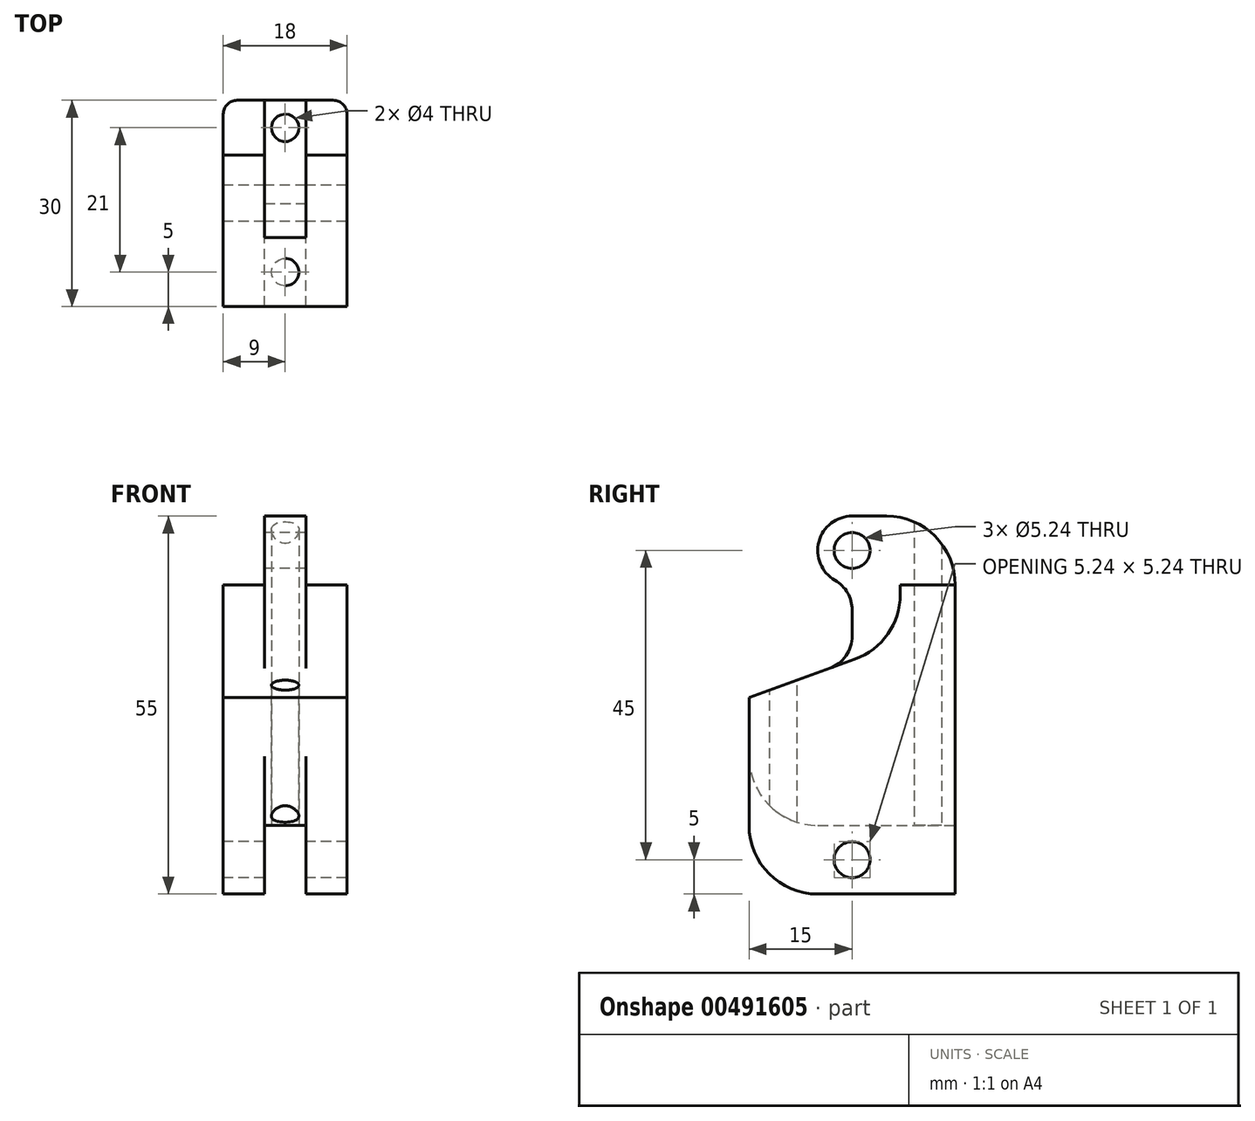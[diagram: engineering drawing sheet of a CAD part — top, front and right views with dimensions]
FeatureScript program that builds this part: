
annotation { "Feature Type Name" : "Feature", "Feature Type Description" : "" }
export const myFeature = defineFeature(function(context is Context, id is Id, definition is map)
    precondition{}
    {
        {
            var Q0;
            Q0=qCreatedBy(makeId("Front.planeOp"),FACE);
            var sketch = newSketch(context, id + "F0", { "sketchPlane" : qUnion([Q0])});
            skLineSegment(sketch, "E0.bottom", {"start": v(9, 17.5) * mm, "end": v(3, 17.5) * mm});
            skLineSegment(sketch, "E0.top", {"start": v(3, -17.5) * mm, "end": v(-3, -17.5) * mm});
            skLineSegment(sketch, "E0.left", {"start": v(9, 17.5) * mm, "end": v(9, -17.5) * mm});
            skLineSegment(sketch, "E0.right", {"start": v(-9, 17.5) * mm, "end": v(-9, -17.5) * mm});
            skPoint(sketch, "E0.middle", {"position": v(0, 0) * mm});
            skLineSegment(sketch, "E1.bottom", {"start": v(3, 27.5) * mm, "end": v(-3, 27.5) * mm});
            skLineSegment(sketch, "E1.left", {"start": v(3, 27.5) * mm, "end": v(3, 17.5) * mm});
            skLineSegment(sketch, "E1.right", {"start": v(-3, 27.5) * mm, "end": v(-3, 17.5) * mm});
            skPoint(sketch, "E1.middle", {"position": v(0, 17.5) * mm});
            skLineSegment(sketch, "E2.top", {"start": v(-9, -27.5) * mm, "end": v(-3, -27.5) * mm});
            skLineSegment(sketch, "E2.right", {"start": v(-3, -17.5) * mm, "end": v(-3, -27.5) * mm});
            skLineSegment(sketch, "E3.MirrorCS", {"start": v(3, -17.5) * mm, "end": v(3, -27.5) * mm});
            skLineSegment(sketch, "E4.MirrorCS", {"start": v(9, -27.5) * mm, "end": v(3, -27.5) * mm});
            skLineSegment(sketch, "E5.MirrorCS", {"start": v(9, -17.5) * mm, "end": v(9, -27.5) * mm});
            skLineSegment(sketch, "E6.trimOffspring", {"start": v(-3, 17.5) * mm, "end": v(-9, 17.5) * mm});
            skLineSegment(sketch, "E7", {"start": v(-9, -17.5) * mm, "end": v(-9, -27.5) * mm});
            skSolve(sketch);
        }
        {
            var Q0;
            Q0=makeQuery(id+"F0.imprint","IMPRINT",FACE,{"disambiguationData":[TD([[makeQuery(id+"F0.imprint","IMPRINT",EDGE,{"derivedFrom":sQuery(id+"F0.wireOp",EDGE,"E0.bottom")}),1.0]])]});
            extrude(context, id + "F1", {"entities" : qUnion([Q0]), "depth" : 30 * mm, "symmetric" : true});
        }
        {
            var Q0;
            Q0=makeQuery(id+"F1.opExtrude","SWEPT_FACE",FACE,{"disambiguationData":[OSD([sQuery(id+"F0.wireOp",EDGE,"E1.right")])]});
            var sketch = newSketch(context, id + "F2", { "sketchPlane" : qUnion([Q0])});
            skLineSegment(sketch, "E8", {"start": v(0, 17.5) * mm, "end": v(0, 27.5) * mm});
            skCircle(sketch, "E9", {"center": v(0, 22.5) * mm, "radius": 2.62 * mm});
            skSolve(sketch);
        }
        {
            var Q0;
            Q0 = qSketchRegion(id + "F2", true);
            extrude(context, id + "F3", {"entities" : qUnion([Q0]), "operationType" : NewBodyOperationType.REMOVE, "oppositeDirection" : true, "depth" : 6 * mm});
        }
        {
            var Q0;
            Q0=makeQuery(id+"F1.opExtrude","SWEPT_FACE",FACE,{"disambiguationData":[OSD([sQuery(id+"F0.wireOp",EDGE,"E0.right"),sQuery(id+"F0.wireOp",EDGE,"E7")])]});
            var sketch = newSketch(context, id + "F4", { "sketchPlane" : qUnion([Q0])});
            skPoint(sketch, "E10.endSnap0", {"position": v(0, -27.5) * mm});
            skCircle(sketch, "E11", {"center": v(0, -22.5) * mm, "radius": 2.62 * mm});
            skLineSegment(sketch, "E12", {"start": v(0, -27.5) * mm, "end": v(0, -22.5) * mm});
            skSolve(sketch);
        }
        {
            var Q0;
            Q0 = qSketchRegion(id + "F4", true);
            extrude(context, id + "F5", {"entities" : qUnion([Q0]), "operationType" : NewBodyOperationType.REMOVE, "oppositeDirection" : true, "depth" : 18 * mm});
        }
        {
            var Q0;
            Q0=makeQuery(id+"F1.opExtrude","CAP_EDGE",EDGE,{"disambiguationData":[OSD([sQuery(id+"F0.wireOp",EDGE,"E1.bottom")])],"isStart":true});
            var Q1;
            Q1=makeQuery(id+"F1.opExtrude","CAP_EDGE",EDGE,{"disambiguationData":[OSD([sQuery(id+"F0.wireOp",EDGE,"E1.bottom")])],"isStart":false});
            var Q2;
            Q2=makeQuery(id+"F1.opExtrude","CAP_EDGE",EDGE,{"disambiguationData":[OSD([sQuery(id+"F0.wireOp",EDGE,"E4.MirrorCS")])],"isStart":false});
            var Q3;
            Q3=makeQuery(id+"F1.opExtrude","CAP_EDGE",EDGE,{"disambiguationData":[OSD([sQuery(id+"F0.wireOp",EDGE,"E2.top")])],"isStart":false});
            fillet(context, id + "F6", {"entities" : qUnion([Q0, Q1, Q2, Q3]), "radius" : 10 * mm, "tangentPropagation" : true, "allowEdgeOverflow" : false});
        }
        {
            var Q0;
            Q0=makeQuery(id+"F1.opExtrude","SWEPT_FACE",FACE,{"disambiguationData":[OSD([sQuery(id+"F0.wireOp",EDGE,"E0.left"),sQuery(id+"F0.wireOp",EDGE,"E5.MirrorCS")])]});
            var sketch = newSketch(context, id + "F7", { "sketchPlane" : qUnion([Q0])});
            skPoint(sketch, "E13.endSnap0", {"position": v(0, 17.5) * mm});
            skLineSegment(sketch, "E14", {"start": v(-15, 17.5) * mm, "end": v(-15, 1.08) * mm});
            skLineSegment(sketch, "E15", {"start": v(-15, 17.5) * mm, "end": v(7, 17.5) * mm});
            skLineSegment(sketch, "E16", {"start": v(-15, 1.08) * mm, "end": v(15, 1.08) * mm});
            skLineSegment(sketch, "E17", {"start": v(-15, 1.08) * mm, "end": v(0.42, 6.7) * mm});
            skLineSegment(sketch, "E18", {"start": v(7, 17.5) * mm, "end": v(7, 16.09) * mm});
            skPoint(sketch, "E19.visualSharp", {"position": v(7, 9.09) * mm});
            skArc(sketch, "E19.filletArc", {"start": v(0.42, 6.7) * mm, "mid": v(5.2, 10.35) * mm, "end": v(7, 16.09) * mm});
            skSolve(sketch);
        }
        {
            var Q0;
            Q0=makeQuery(id+"F1.opExtrude","SWEPT_FACE",FACE,{"disambiguationData":[OSD([sQuery(id+"F0.wireOp",EDGE,"E0.right"),sQuery(id+"F0.wireOp",EDGE,"E7")])]});
            var sketch = newSketch(context, id + "F8", { "sketchPlane" : qUnion([Q0])});
            skLineSegment(sketch, "E20", {"start": v(-0.42, 6.7) * mm, "end": v(15, 1.08) * mm});
            skLineSegment(sketch, "E21", {"start": v(15, 1.08) * mm, "end": v(15, 17.5) * mm});
            skLineSegment(sketch, "E22", {"start": v(15, 1.08) * mm, "end": v(-15, 1.08) * mm});
            skLineSegment(sketch, "E23", {"start": v(15, 17.5) * mm, "end": v(-7, 17.5) * mm});
            skLineSegment(sketch, "E24", {"start": v(-7, 17.5) * mm, "end": v(-7, 16.09) * mm});
            skPoint(sketch, "E25.visualSharp", {"position": v(-7, 9.09) * mm});
            skArc(sketch, "E25.filletArc", {"start": v(-7, 16.09) * mm, "mid": v(-5.2, 10.35) * mm, "end": v(-0.42, 6.7) * mm});
            skSolve(sketch);
        }
        {
            var Q0;
            Q0=makeQuery(id+"F8.imprint","IMPRINT",FACE,{"disambiguationData":[TD([[makeQuery(id+"F8.imprint","IMPRINT",EDGE,{"derivedFrom":sQuery(id+"F8.wireOp",EDGE,"E20")}),1.0]])]});
            extrude(context, id + "F9", {"entities" : qUnion([Q0]), "operationType" : NewBodyOperationType.REMOVE, "oppositeDirection" : true, "depth" : 6 * mm});
        }
        {
            var Q0;
            Q0=makeQuery(id+"F7.imprint","IMPRINT",FACE,{"disambiguationData":[TD([[makeQuery(id+"F7.imprint","IMPRINT",EDGE,{"derivedFrom":sQuery(id+"F7.wireOp",EDGE,"E14")}),1.0]])]});
            extrude(context, id + "F10", {"entities" : qUnion([Q0]), "operationType" : NewBodyOperationType.REMOVE, "oppositeDirection" : true, "depth" : 6 * mm});
        }
        {
            var Q0;
            Q0=makeQuery(id+"F1.opExtrude","CAP_EDGE",EDGE,{"disambiguationData":[OSD([sQuery(id+"F0.wireOp",EDGE,"E0.left"),sQuery(id+"F0.wireOp",EDGE,"E5.MirrorCS")])],"isStart":true});
            var Q1;
            Q1=makeQuery(id+"F1.opExtrude","CAP_EDGE",EDGE,{"disambiguationData":[OSD([sQuery(id+"F0.wireOp",EDGE,"E0.right"),sQuery(id+"F0.wireOp",EDGE,"E7")])],"isStart":true});
            fillet(context, id + "F11", {"entities" : qUnion([Q0, Q1]), "radius" : 2 * mm, "tangentPropagation" : true, "allowEdgeOverflow" : false});
        }
        {
            var Q0;
            Q0=makeQuery(id+"F9.boolean.opBoolean","MERGE",FACE,{"derivedFrom":[makeQuery(id+"F1.opExtrude","SWEPT_FACE",FACE,{"disambiguationData":[OSD([sQuery(id+"F0.wireOp",EDGE,"E1.right")])]}),makeQuery(id+"F9.opExtrude","CAP_FACE",FACE,{"disambiguationData":[OSD([sQuery(id+"F8.wireOp",EDGE,"E20"),sQuery(id+"F8.wireOp",EDGE,"E21"),sQuery(id+"F8.wireOp",EDGE,"E23"),sQuery(id+"F8.wireOp",EDGE,"E24"),sQuery(id+"F8.wireOp",EDGE,"E25.filletArc")])],"isStart":false})]});
            var sketch = newSketch(context, id + "F12", { "sketchPlane" : qUnion([Q0])});
            skLineSegment(sketch, "E26", {"start": v(0, 27.5) * mm, "end": v(0, 25.12) * mm});
            skCircle(sketch, "E27", {"center": v(0, 22.5) * mm, "radius": 5 * mm});
            skLineSegment(sketch, "E28", {"start": v(0, 22.5) * mm, "end": v(5, 22.5) * mm});
            skLineSegment(sketch, "E29", {"start": v(5, 22.5) * mm, "end": v(5, 4.72) * mm});
            skSolve(sketch);
        }
        {
            var Q0;
            {var subQ1=sQuery(id+"F12.wireOp",EDGE,"E29");Q0=makeQuery(id+"F12.imprint","IMPRINT",FACE,{"disambiguationData":[TD([[makeQuery(id+"F12.imprint","IMPRINT",EDGE,{"derivedFrom":subQ1}),1.0]])]});}
            extrude(context, id + "F13", {"entities" : qUnion([Q0]), "operationType" : NewBodyOperationType.REMOVE, "oppositeDirection" : true, "depth" : 6 * mm});
        }
        {
            var Q0;
            Q0=makeQuery(id+"F1.opExtrude","SWEPT_FACE",FACE,{"disambiguationData":[OSD([sQuery(id+"F0.wireOp",EDGE,"E0.top")])]});
            var sketch = newSketch(context, id + "F14", { "sketchPlane" : qUnion([Q0])});
            skSolve(sketch);
        }
        {
            var Q0;
            Q0=makeQuery(id+"F1.opExtrude","CAP_EDGE",EDGE,{"disambiguationData":[OSD([sQuery(id+"F0.wireOp",EDGE,"E0.top")])],"isStart":false});
            fillet(context, id + "F15", {"entities" : qUnion([Q0]), "radius" : 10 * mm, "tangentPropagation" : true, "allowEdgeOverflow" : false});
        }
        {
            var Q0;
            {var subQ0=sQuery(id+"F8.wireOp",EDGE,"E20");Q0=makeQuery(id+"F13.boolean.opBoolean","MERGE",FACE,{"derivedFrom":[makeQuery(id+"F9.boolean.opBoolean","COPY",FACE,{"derivedFrom":makeQuery(id+"F9.opExtrude","SWEPT_FACE",FACE,{"disambiguationData":[OSD([subQ0])]})}),makeQuery(id+"F10.boolean.opBoolean","COPY",FACE,{"derivedFrom":makeQuery(id+"F10.opExtrude","SWEPT_FACE",FACE,{"disambiguationData":[OSD([sQuery(id+"F7.wireOp",EDGE,"E17")])]})}),makeQuery(id+"F13.opExtrude","SWEPT_FACE",FACE,{"disambiguationData":[OSD([subQ0])]})]});}
            var sketch = newSketch(context, id + "F16", { "sketchPlane" : qUnion([Q0])});
            skLineSegment(sketch, "E30", {"start": v(0, -3.08) * mm, "end": v(0, -13.73) * mm});
            skSolve(sketch);
        }
        {
            var Q0;
            Q0=makeQuery(id+"F13.boolean.opBoolean","COPY",EDGE,{"derivedFrom":makeQuery(id+"F13.opExtrude","SWEPT_EDGE",EDGE,{"disambiguationData":[OSD([sQuery(id+"F12.wireOp",EDGE,"E27"),sQuery(id+"F12.wireOp",EDGE,"E28"),sQuery(id+"F12.wireOp",EDGE,"E29")])]})});
            cPlane(context, id + "F17", {"entities" : qUnion([Q0]), "cplaneType" : CPlaneType.LINE_ANGLE, "offset" : 25 * mm, "angle" : 90 * degree, "width" : 150 * mm, "height" : 150 * mm});
        }
        {
            var Q0;
            Q0=qCreatedBy(id+"F17.planeOp",FACE);
            var sketch = newSketch(context, id + "F18", { "sketchPlane" : qUnion([Q0])});
            skLineSegment(sketch, "E31", {"start": v(0, -5) * mm, "end": v(0, -15) * mm});
            skCircle(sketch, "E32", {"center": v(0, -10) * mm, "radius": 2 * mm});
            skSolve(sketch);
        }
        {
            var Q0;
            Q0 = qSketchRegion(id + "F18", true);
            extrude(context, id + "F19", {"entities" : qUnion([Q0]), "operationType" : NewBodyOperationType.REMOVE, "endBound" : BoundingType.THROUGH_ALL, "oppositeDirection" : true, "depth" : 40 * mm});
        }
        {
            var Q0;
            {var subQ0=sQuery(id+"F0.wireOp",EDGE,"E0.top");Q0=makeQuery(id+"F14.imprint","IMPRINT",FACE,{"disambiguationData":[TD([[makeQuery(id+"F14.imprint","IMPRINT",EDGE,{"derivedFrom":makeQuery(id+"F1.opExtrude","CAP_EDGE",EDGE,{"disambiguationData":[OSD([subQ0])],"isStart":true})}),-1.0]])]});}
            var sketch = newSketch(context, id + "F20", { "sketchPlane" : qUnion([Q0])});
            skLineSegment(sketch, "E33", {"start": v(0, -15) * mm, "end": v(0, -11) * mm});
            skCircle(sketch, "E34", {"center": v(0, -11) * mm, "radius": 2 * mm});
            skLineSegment(sketch, "E35", {"start": v(0, -11) * mm, "end": v(0, -7.51) * mm});
            skSolve(sketch);
        }
        {
            var Q0;
            {var subQ0=sQuery(id+"F20.wireOp",EDGE,"E35");var subQ1=sQuery(id+"F20.wireOp",EDGE,"E33");var subQ2=makeQuery(id+"F20.imprint","INTERSECT",VERTEX,{"derivedFrom":[subQ1,subQ0]});Q0=makeQuery(id+"F20.imprint","IMPRINT",FACE,{"disambiguationData":[TD([[makeQuery(id+"F20.imprint","IMPRINT",EDGE,{"disambiguationData":[TD([[subQ2,1.0]])],"derivedFrom":subQ1}),1.0]])]});}
            var Q1;
            {var subQ0=sQuery(id+"F20.wireOp",EDGE,"E35");var subQ1=sQuery(id+"F20.wireOp",EDGE,"E33");var subQ2=makeQuery(id+"F20.imprint","INTERSECT",VERTEX,{"derivedFrom":[subQ1,subQ0]});Q1=makeQuery(id+"F20.imprint","IMPRINT",FACE,{"disambiguationData":[TD([[makeQuery(id+"F20.imprint","IMPRINT",EDGE,{"disambiguationData":[TD([[subQ2,1.0]])],"derivedFrom":subQ1}),-1.0]])]});}
            extrude(context, id + "F21", {"entities" : qUnion([Q0, Q1]), "operationType" : NewBodyOperationType.REMOVE, "endBound" : BoundingType.THROUGH_ALL, "oppositeDirection" : true, "depth" : 50 * mm});
        }
        {
            var Q0;
            Q0=makeQuery(id+"F10.boolean.opBoolean","MERGE",FACE,{"derivedFrom":[makeQuery(id+"F1.opExtrude","SWEPT_FACE",FACE,{"disambiguationData":[OSD([sQuery(id+"F0.wireOp",EDGE,"E1.left")])]}),makeQuery(id+"F10.opExtrude","CAP_FACE",FACE,{"disambiguationData":[OSD([sQuery(id+"F7.wireOp",EDGE,"E14"),sQuery(id+"F7.wireOp",EDGE,"E15"),sQuery(id+"F7.wireOp",EDGE,"E17"),sQuery(id+"F7.wireOp",EDGE,"E18"),sQuery(id+"F7.wireOp",EDGE,"E19.filletArc")])],"isStart":false})]});
            var sketch = newSketch(context, id + "F22", { "sketchPlane" : qUnion([Q0])});
            skArc(sketch, "E36", {"start": v(-5, 22.5) * mm, "mid": v(-3.54, 18.96) * mm, "end": v(0, 17.5) * mm});
            skLineSegment(sketch, "E37", {"start": v(0, 17.5) * mm, "end": v(0, 6.54) * mm});
            skLineSegment(sketch, "E38", {"start": v(0, 6.54) * mm, "end": v(-5, 4.72) * mm});
            skLineSegment(sketch, "E39", {"start": v(-5, 4.72) * mm, "end": v(-5, 22.5) * mm});
            skSolve(sketch);
        }
        {
            var Q0;
            Q0=makeQuery(id+"F22.imprint","IMPRINT",FACE,{"disambiguationData":[TD([[makeQuery(id+"F22.imprint","IMPRINT",EDGE,{"derivedFrom":sQuery(id+"F22.wireOp",EDGE,"E36")}),-1.0]])]});
            extrude(context, id + "F23", {"entities" : qUnion([Q0]), "operationType" : NewBodyOperationType.REMOVE, "oppositeDirection" : true, "depth" : 6 * mm});
        }
        {
            var Q0;
            Q0=makeQuery(id+"F23.boolean.opBoolean","COPY",EDGE,{"derivedFrom":makeQuery(id+"F23.opExtrude","SWEPT_EDGE",EDGE,{"disambiguationData":[OSD([sQuery(id+"F22.wireOp",EDGE,"E36"),sQuery(id+"F22.wireOp",EDGE,"E37")])]})});
            var Q1;
            Q1=makeQuery(id+"F23.boolean.opBoolean","COPY",EDGE,{"derivedFrom":makeQuery(id+"F23.opExtrude","SWEPT_EDGE",EDGE,{"disambiguationData":[OSD([sQuery(id+"F7.wireOp",EDGE,"E17"),sQuery(id+"F22.wireOp",EDGE,"E37"),sQuery(id+"F22.wireOp",EDGE,"E38")])]})});
            fillet(context, id + "F24", {"entities" : qUnion([Q0, Q1]), "radius" : 5 * mm, "tangentPropagation" : true, "allowEdgeOverflow" : false});
        }
    });
